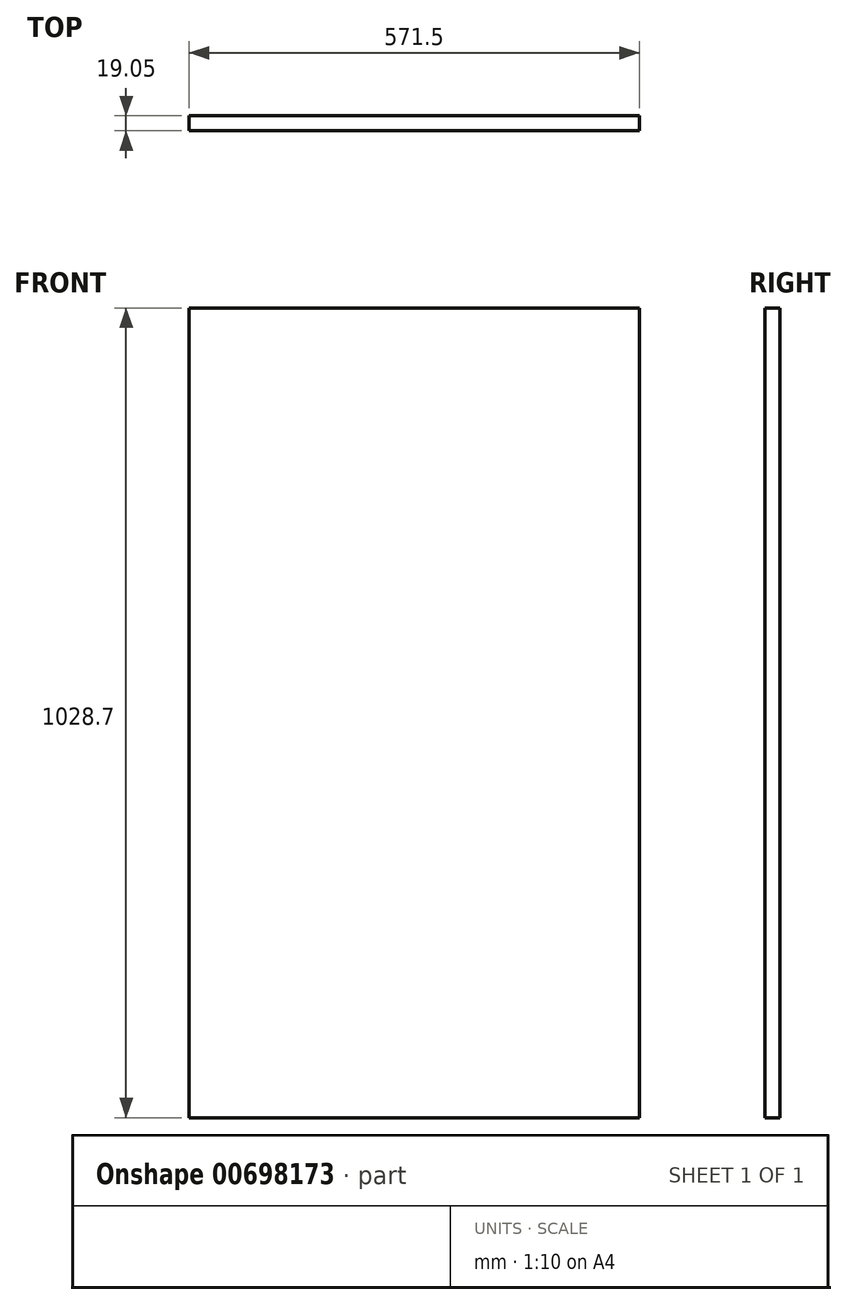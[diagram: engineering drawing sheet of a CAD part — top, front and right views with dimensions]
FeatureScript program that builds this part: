
annotation { "Feature Type Name" : "Feature", "Feature Type Description" : "" }
export const myFeature = defineFeature(function(context is Context, id is Id, definition is map)
    precondition{}
    {
        {
            var Q0;
            Q0=qCreatedBy(makeId("Front.planeOp"),FACE);
            var sketch = newSketch(context, id + "F0", { "sketchPlane" : qUnion([Q0])});
            skLineSegment(sketch, "E0.bottom", {"start": v(285.75, 514.35) * mm, "end": v(-285.75, 514.35) * mm});
            skLineSegment(sketch, "E0.top", {"start": v(285.75, -514.35) * mm, "end": v(-285.75, -514.35) * mm});
            skLineSegment(sketch, "E0.left", {"start": v(285.75, 514.35) * mm, "end": v(285.75, -514.35) * mm});
            skLineSegment(sketch, "E0.right", {"start": v(-285.75, 514.35) * mm, "end": v(-285.75, -514.35) * mm});
            skPoint(sketch, "E0.middle", {"position": v(0, 0) * mm});
            skSolve(sketch);
        }
        {
            var Q0;
            Q0=makeQuery(id+"F0.imprint","IMPRINT",FACE,{"disambiguationData":[TD([[makeQuery(id+"F0.imprint","IMPRINT",EDGE,{"derivedFrom":sQuery(id+"F0.wireOp",EDGE,"E0.bottom")}),1.0]])]});
            extrude(context, id + "F1", {"entities" : qUnion([Q0]), "depth" : 19.05 * mm, "offsetDistance" : 25.4 * mm});
        }
    });
